# Revit family: Thorn E-FACT
name_source: partatom
category: Lighting Fixtures
revit_build: Autodesk Revit 2016 (Build: 20150220_1215(x64)
units: mm (PartAtom-declared; Revit-internal decimal feet)

## family parameters
Cut with Voids When Loaded = No
Host = Face
Light Source = Yes
OmniClass Number = 23.80.70.11
OmniClass Title = Luminaries for Internal Lighting
Part Type = Normal
Room Calculation Point = No
Round Connector Dimension = Use Diameter
Shared = No

## types (1)
- E/Fact / EFACT R00 1L35 SOFT BLU AL FR
    Apparent Load = 2 VA
    Assembly Code = D5020200
    Body = Thorn_Metal_Dark_Grey
    Color Filter = 16777215
    Cover = Thorn_Metal_Aluminium
    Default Elevation = 0 mm  [stored 0 ft]
    Description = LED recessed luminaire
    Dimming Lamp Color Temperature Shift = <None>
    Emit Shape Visible in Rendering = No
    Emit from Circle Diameter = 45 mm  [stored 0.147638 ft]
    Height = 112 mm
    Lamp = LED
    Length = 85 mm
    Manufacturer = Thorn Lighting
    Model = 96271569
    Photometric Web File = 96271569_(STD).IES
    Reflector = Thorn_Glass_Self_llumination_Transparent
    Tilt Angle = -90.00°
    URL = www.thornlighting.com/96271569
    Voltage = 230 V
    Width = 85 mm

note: [stored X ft] marks values corroborated as IEEE doubles in the binary element streams (Revit-internal decimal feet)

## geometry (parser evidence)
native form markers: Sweep x3
no freeform markers — native parametric forms only
